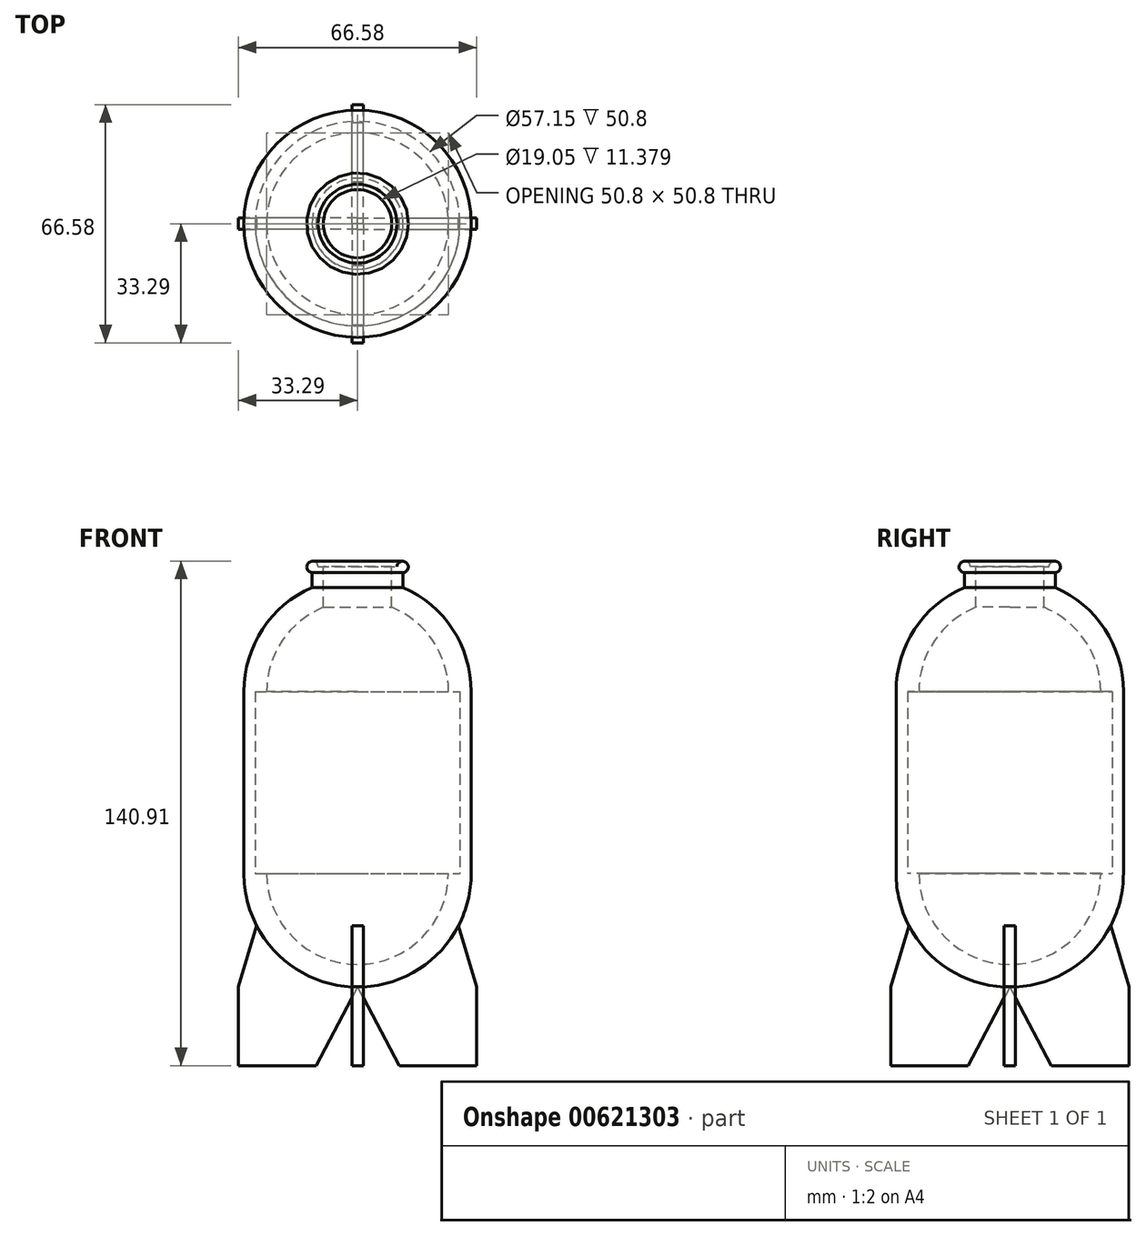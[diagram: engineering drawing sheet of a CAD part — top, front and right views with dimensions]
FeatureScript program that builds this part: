
annotation { "Feature Type Name" : "Feature", "Feature Type Description" : "" }
export const myFeature = defineFeature(function(context is Context, id is Id, definition is map)
    precondition{}
    {
        {
            var Q0;
            Q0=qCreatedBy(makeId("Top.planeOp"),FACE);
            var sketch = newSketch(context, id + "F0", { "sketchPlane" : qUnion([Q0])});
            skCircle(sketch, "E0", {"center": v(0, 0) * mm, "radius": 31.75 * mm});
            skCircle(sketch, "E1", {"center": v(0, 0) * mm, "radius": 28.58 * mm});
            skSolve(sketch);
        }
        {
            var Q0;
            Q0=qSketchRegion(id+"F0",true);
            extrude(context, id + "F1", {"entities" : qUnion([Q0]), "endBound" : BoundingType.SYMMETRIC, "depth" : 50.8 * mm});
        }
        {
            var Q0;
            Q0=makeQuery(id+"F1.opExtrude","CAP_FACE",FACE,{"disambiguationData":[OSD([sQuery(id+"F0.wireOp",EDGE,"E0"),sQuery(id+"F0.wireOp",EDGE,"E1")])],"isStart":false});
            var sketch = newSketch(context, id + "F2", { "sketchPlane" : qUnion([Q0])});
            skArc(sketch, "E2", {"start": v(0, -31.75) * mm, "mid": v(31.75, 0) * mm, "end": v(0, 31.75) * mm});
            skArc(sketch, "E3", {"start": v(0, -25.4) * mm, "mid": v(25.4, 0) * mm, "end": v(0, 25.4) * mm});
            skLineSegment(sketch, "E4", {"start": v(0, 31.75) * mm, "end": v(0, -31.75) * mm, "construction": true});
            skLineSegment(sketch, "E5", {"start": v(0, 31.75) * mm, "end": v(0, 25.4) * mm});
            skLineSegment(sketch, "E6", {"start": v(0, -31.75) * mm, "end": v(0, -25.4) * mm});
            skSolve(sketch);
        }
        {
            var Q0;
            Q0=qSketchRegion(id+"F2",true);
            var Q1;
            Q1=sQuery(id+"F2.wireOp",EDGE,"E4");
            revolve(context, id + "F3", {"operationType" : NewBodyOperationType.ADD, "entities" : qUnion([Q0]), "axis" : qUnion([Q1]), "revolveType" : RevolveType.ONE_DIRECTION, "angle" : 180 * degree});
        }
        {
            var Q0;
            Q0=makeQuery(id+"F1.opExtrude","SWEPT_BODY",BODY,{"disambiguationData":[OSD([sQuery(id+"F0.wireOp",EDGE,"E0"),sQuery(id+"F0.wireOp",EDGE,"E1")])]});
            var Q1;
            Q1=qCreatedBy(makeId("Top.planeOp"),FACE);
            mirror(context, id + "F4", {"operationType" : NewBodyOperationType.ADD, "entities" : qUnion([Q0]), "mirrorPlane" : qUnion([Q1])});
        }
        {
            var Q0;
            Q0=qCreatedBy(makeId("Top.planeOp"),FACE);
            cPlane(context, id + "F5", {"entities" : qUnion([Q0]), "cplaneType" : CPlaneType.OFFSET, "offset" : 57.15 * mm, "width" : 152.4 * mm, "height" : 152.4 * mm});
        }
        {
            var Q0;
            Q0=qCreatedBy(id+"F5.planeOp",FACE);
            var sketch = newSketch(context, id + "F6", { "sketchPlane" : qUnion([Q0])});
            skCircle(sketch, "E7", {"center": v(0, 0) * mm, "radius": 12.7 * mm});
            skSolve(sketch);
        }
        {
            var Q0;
            Q0=qSketchRegion(id+"F6",true);
            extrude(context, id + "F7", {"entities" : qUnion([Q0]), "operationType" : NewBodyOperationType.ADD, "endBound" : BoundingType.SYMMETRIC, "depth" : 6.35 * mm});
        }
        {
            var Q0;
            Q0=makeQuery(id+"F7.opExtrude","CAP_FACE",FACE,{"disambiguationData":[OSD([sQuery(id+"F6.wireOp",EDGE,"E7")])],"isStart":false});
            var sketch = newSketch(context, id + "F8", { "sketchPlane" : qUnion([Q0])});
            skCircle(sketch, "E8", {"center": v(0, 0) * mm, "radius": 9.53 * mm});
            skSolve(sketch);
        }
        {
            var Q0;
            Q0=qSketchRegion(id+"F8",true);
            extrude(context, id + "F9", {"entities" : qUnion([Q0]), "operationType" : NewBodyOperationType.REMOVE, "oppositeDirection" : true, "depth" : 25.4 * mm});
        }
        {
            var Q0;
            Q0=qCreatedBy(makeId("Front.planeOp"),FACE);
            var sketch = newSketch(context, id + "F10", { "sketchPlane" : qUnion([Q0])});
            skArc(sketch, "E9", {"start": v(0, -57.15) * mm, "mid": v(16.5, -52.53) * mm, "end": v(28.2, -40) * mm});
            skLineSegment(sketch, "E10", {"start": v(0, -57.15) * mm, "end": v(11.6, -79.09) * mm});
            skLineSegment(sketch, "E11", {"start": v(11.6, -79.09) * mm, "end": v(33.29, -79.09) * mm});
            skLineSegment(sketch, "E12", {"start": v(33.29, -79.09) * mm, "end": v(33.29, -57.05) * mm});
            skLineSegment(sketch, "E13", {"start": v(33.29, -57.05) * mm, "end": v(28.2, -40) * mm});
            skPoint(sketch, "E14.orphan", {"position": v(31.75, -25.4) * mm});
            skPoint(sketch, "E15.orphan", {"position": v(-31.75, -25.4) * mm});
            skSolve(sketch);
        }
        {
            var Q0;
            Q0=qSketchRegion(id+"F10",true);
            extrude(context, id + "F11", {"entities" : qUnion([Q0]), "operationType" : NewBodyOperationType.ADD, "endBound" : BoundingType.SYMMETRIC, "depth" : 3.17 * mm});
        }
        {
            var Q0;
            Q0=qCreatedBy(makeId("Right.planeOp"),FACE);
            var sketch = newSketch(context, id + "F12", { "sketchPlane" : qUnion([Q0])});
            skLineSegment(sketch, "E16", {"start": v(0, 60.8) * mm, "end": v(0, -57.24) * mm, "construction": true});
            skSolve(sketch);
        }
        {
            var Q0;
            Q0=makeQuery(id+"F11.opExtrude","SWEPT_BODY",BODY,{"disambiguationData":[OSD([sQuery(id+"F10.wireOp",EDGE,"E9"),sQuery(id+"F10.wireOp",EDGE,"E10"),sQuery(id+"F10.wireOp",EDGE,"E11"),sQuery(id+"F10.wireOp",EDGE,"E12"),sQuery(id+"F10.wireOp",EDGE,"E13")])]});
            var Q1;
            Q1=sQuery(id+"F12.wireOp",EDGE,"E16");
            circularPattern(context, id + "F13", {"entities" : qUnion([Q0]), "axis" : qUnion([Q1]), "angle" : 90 * degree, "instanceCount" : 4});
        }
        {
            var Q0;
            Q0=qCreatedBy(makeId("Front.planeOp"),FACE);
            var sketch = newSketch(context, id + "F14", { "sketchPlane" : qUnion([Q0])});
            skLineSegment(sketch, "E17", {"start": v(0, 46.85) * mm, "end": v(0, 31.4) * mm, "construction": true});
            skCircle(sketch, "E18", {"center": v(12.6, 60.23) * mm, "radius": 1.59 * mm});
            skSolve(sketch);
        }
        {
            var Q0;
            Q0=qSketchRegion(id+"F14",true);
            var Q1;
            Q1=sQuery(id+"F14.wireOp",EDGE,"E17");
            revolve(context, id + "F15", {"operationType" : NewBodyOperationType.ADD, "entities" : qUnion([Q0]), "axis" : qUnion([Q1]), "revolveType" : RevolveType.FULL});
        }
    });
